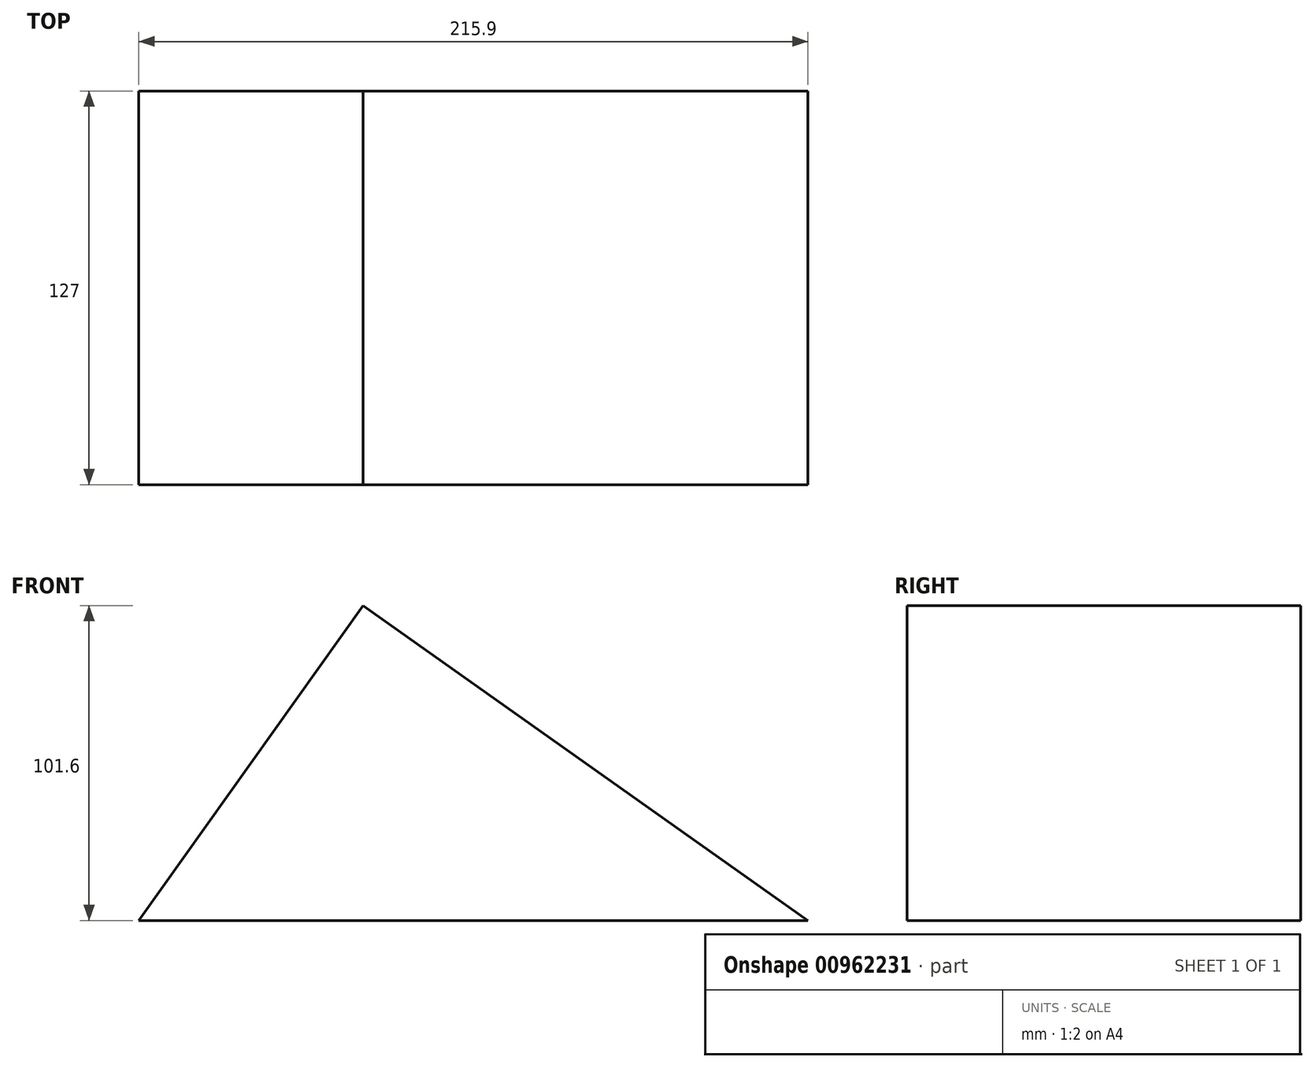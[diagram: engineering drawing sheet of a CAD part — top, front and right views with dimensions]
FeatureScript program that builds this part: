
annotation { "Feature Type Name" : "Feature", "Feature Type Description" : "" }
export const myFeature = defineFeature(function(context is Context, id is Id, definition is map)
    precondition{}
    {
        {
            var Q0;
            Q0=qCreatedBy(makeId("Front.planeOp"),FACE);
            var sketch = newSketch(context, id + "F0", { "sketchPlane" : qUnion([Q0])});
            skLineSegment(sketch, "E0", {"start": v(0, 101.6) * mm, "end": v(-72.33, 0) * mm});
            skLineSegment(sketch, "E1", {"start": v(-72.33, 0) * mm, "end": v(143.57, 0) * mm});
            skLineSegment(sketch, "E2", {"start": v(143.57, 0) * mm, "end": v(0, 101.6) * mm});
            skSolve(sketch);
        }
        {
            var Q0;
            Q0=makeQuery(id+"F0.imprint","IMPRINT",FACE,{"disambiguationData":[TD([[makeQuery(id+"F0.imprint","IMPRINT",EDGE,{"derivedFrom":sQuery(id+"F0.wireOp",EDGE,"E0")}),1.0]])]});
            extrude(context, id + "F1", {"entities" : qUnion([Q0]), "depth" : 127 * mm, "offsetDistance" : 25.4 * mm});
        }
    });
